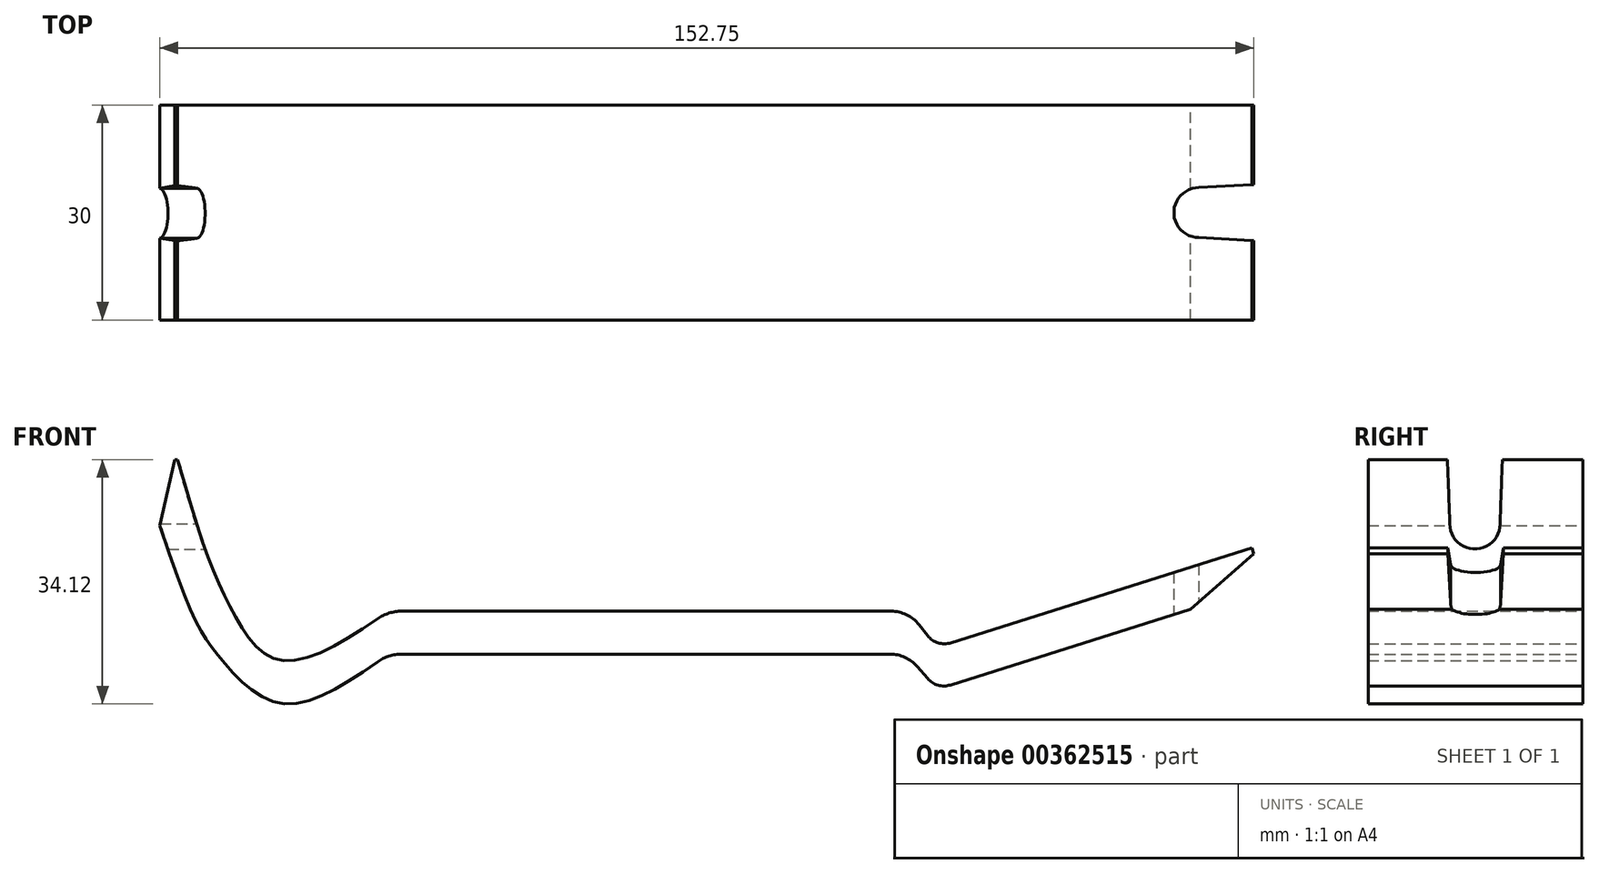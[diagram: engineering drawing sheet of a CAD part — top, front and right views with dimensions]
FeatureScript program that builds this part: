
annotation { "Feature Type Name" : "Feature", "Feature Type Description" : "" }
export const myFeature = defineFeature(function(context is Context, id is Id, definition is map)
    precondition{}
    {
        {
            var Q0;
            Q0=qCreatedBy(makeId("Front.planeOp"),FACE);
            var sketch = newSketch(context, id + "F0", { "sketchPlane" : qUnion([Q0])});
            skLineSegment(sketch, "E0", {"start": v(74.68, -0.65) * mm, "end": v(-75.32, -0.65) * mm, "construction": true});
            skFitSpline(sketch, "E1", {"points": [v(-75.32, 17.3) * mm, v(-67.32, -0.65) * mm, v(-58.65, -7.47) * mm, v(-43.4, -0.65) * mm], "startDerivative": vector(34.89, -102.7) * mm, "endDerivative": vector(49.86, 35.36) * mm});
            skLineSegment(sketch, "E2", {"start": v(31.9, -4.06) * mm, "end": v(30.44, -2.37) * mm});
            skLineSegment(sketch, "E3", {"start": v(26.66, -0.65) * mm, "end": v(-41.5, -0.65) * mm});
            skPoint(sketch, "E4.visualSharp", {"position": v(33.2, -5.55) * mm});
            skArc(sketch, "E4.filletArc", {"start": v(31.9, -4.06) * mm, "mid": v(33.36, -4.99) * mm, "end": v(35.07, -4.96) * mm});
            skArc(sketch, "E5.filletArc", {"start": v(-41.5, -0.65) * mm, "mid": v(-43.31, -0.93) * mm, "end": v(-44.95, -1.74) * mm});
            skPoint(sketch, "E6.visualSharp", {"position": v(28.94, -0.65) * mm});
            skArc(sketch, "E6.filletArc", {"start": v(30.44, -2.37) * mm, "mid": v(28.74, -1.1) * mm, "end": v(26.66, -0.65) * mm});
            skLineSegment(sketch, "E7", {"start": v(26.66, -0.65) * mm, "end": v(26.66, 5.35) * mm, "construction": true});
            skLineSegment(sketch, "E8", {"start": v(77.17, 5.35) * mm, "end": v(-72.83, 5.35) * mm, "construction": true});
            skFitSpline(sketch, "E9", {"points": [v(-72.83, 26.53) * mm, v(-65.2, 5.35) * mm, v(-58.65, -1.47) * mm, v(-43.4, 5.35) * mm], "startDerivative": vector(23.88, -86.05) * mm, "endDerivative": vector(49.86, 35.36) * mm});
            skLineSegment(sketch, "E10", {"start": v(77.17, 14.19) * mm, "end": v(35.16, 0.94) * mm});
            skLineSegment(sketch, "E11", {"start": v(31.9, 1.94) * mm, "end": v(30.7, 3.46) * mm});
            skLineSegment(sketch, "E12", {"start": v(26.78, 5.35) * mm, "end": v(-41.52, 5.35) * mm});
            skPoint(sketch, "E13.visualSharp", {"position": v(33.19, 0.32) * mm});
            skArc(sketch, "E13.filletArc", {"start": v(31.9, 1.94) * mm, "mid": v(33.38, 0.93) * mm, "end": v(35.16, 0.94) * mm});
            skArc(sketch, "E14.filletArc", {"start": v(-41.52, 5.35) * mm, "mid": v(-43.3, 5.08) * mm, "end": v(-44.93, 4.28) * mm});
            skPoint(sketch, "E15.visualSharp", {"position": v(29.2, 5.35) * mm});
            skArc(sketch, "E15.filletArc", {"start": v(30.7, 3.46) * mm, "mid": v(28.96, 4.85) * mm, "end": v(26.78, 5.35) * mm});
            skLineSegment(sketch, "E16", {"start": v(26.78, 5.35) * mm, "end": v(26.78, 11.35) * mm, "construction": true});
            skLineSegment(sketch, "E17", {"start": v(68.62, 5.62) * mm, "end": v(35.07, -4.96) * mm});
            skLineSegment(sketch, "E18", {"start": v(77.17, 14.19) * mm, "end": v(77.43, 13.35) * mm});
            skLineSegment(sketch, "E19", {"start": v(77.43, 13.35) * mm, "end": v(68.62, 5.62) * mm});
            skLineSegment(sketch, "E20", {"start": v(-72.83, 26.53) * mm, "end": v(-73.27, 26.53) * mm});
            skLineSegment(sketch, "E21", {"start": v(-73.27, 26.53) * mm, "end": v(-75.32, 17.3) * mm});
            skSolve(sketch);
        }
        {
            var Q0;
            Q0 = qSketchRegion(id + "F0", true);
            extrude(context, id + "F1", {"entities" : qUnion([Q0]), "depth" : 30 * mm});
        }
        {
            var Q0;
            Q0=qCreatedBy(makeId("Right.planeOp"),FACE);
            var sketch = newSketch(context, id + "F2", { "sketchPlane" : qUnion([Q0])});
            skLineSegment(sketch, "E22", {"start": v(-15.1, 24.52) * mm, "end": v(-15.1, 12.25) * mm, "construction": true});
            skCircle(sketch, "E23", {"center": v(-15.1, 17.53) * mm, "radius": 3.5 * mm, "construction": true});
            skArc(sketch, "E24", {"start": v(-11.6, 17.53) * mm, "mid": v(-15.1, 14.03) * mm, "end": v(-18.6, 17.53) * mm});
            skLineSegment(sketch, "E25", {"start": v(-11.6, 17.53) * mm, "end": v(-11.25, 26.76) * mm});
            skLineSegment(sketch, "E26.MirrorCS", {"start": v(-18.6, 17.53) * mm, "end": v(-18.95, 26.76) * mm});
            skLineSegment(sketch, "E27", {"start": v(-11.25, 26.76) * mm, "end": v(-18.95, 26.76) * mm});
            skSolve(sketch);
        }
        {
            var Q0;
            Q0 = qSketchRegion(id + "F2", true);
            extrude(context, id + "F3", {"entities" : qUnion([Q0]), "operationType" : NewBodyOperationType.REMOVE, "oppositeDirection" : true, "depth" : 80 * mm, "hasSecondDirection" : true, "secondDirectionOppositeDirection" : true, "secondDirectionDepth" : 60 * mm});
        }
        {
            var Q0;
            Q0=qCreatedBy(makeId("Top.planeOp"),FACE);
            var sketch = newSketch(context, id + "F4", { "sketchPlane" : qUnion([Q0])});
            skLineSegment(sketch, "E28", {"start": v(82, -15) * mm, "end": v(57.65, -15) * mm, "construction": true});
            skCircle(sketch, "E29", {"center": v(69.78, -15) * mm, "radius": 3.5 * mm, "construction": true});
            skArc(sketch, "E30", {"start": v(69.78, -11.5) * mm, "mid": v(66.28, -15) * mm, "end": v(69.78, -18.5) * mm});
            skLineSegment(sketch, "E31", {"start": v(69.78, -11.5) * mm, "end": v(78.27, -11.05) * mm});
            skLineSegment(sketch, "E32.MirrorCS", {"start": v(69.78, -18.5) * mm, "end": v(78.27, -18.95) * mm});
            skLineSegment(sketch, "E33", {"start": v(78.27, -11.05) * mm, "end": v(78.27, -18.95) * mm});
            skSolve(sketch);
        }
        {
            var Q0;
            Q0 = qSketchRegion(id + "F4", true);
            extrude(context, id + "F5", {"entities" : qUnion([Q0]), "operationType" : NewBodyOperationType.REMOVE, "depth" : 15 * mm});
        }
    });
